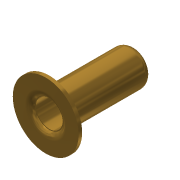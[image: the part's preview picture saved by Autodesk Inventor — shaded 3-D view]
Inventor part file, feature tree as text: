
AUTODESK INVENTOR PART (.ipt)
format: ipt  version: 2013 (Build 170138000, 138)  size: 107,008 bytes
history: native  units: in
note: dims shown in document units (in); Inventor stores cm internally (conversion verified against a paired STEP export)
features: fillet x1, other x1, imported_body x1
ambient origin geometry x8: Origin, YZ Plane, XZ Plane, XY Plane, X Axis, Y Axis, Z Axis, Center Point
feature tree (3):
  fillet  "Fillet1"  [1 undecoded]
  other  "217-2584-005 Rev1 A1"
  imported_body  "Base1"
note: 1 required parameter value undecoded (feature->parameter linkage not recoverable at this tier; creation-order binding heuristic only, values carry confidence <= 0.55)
